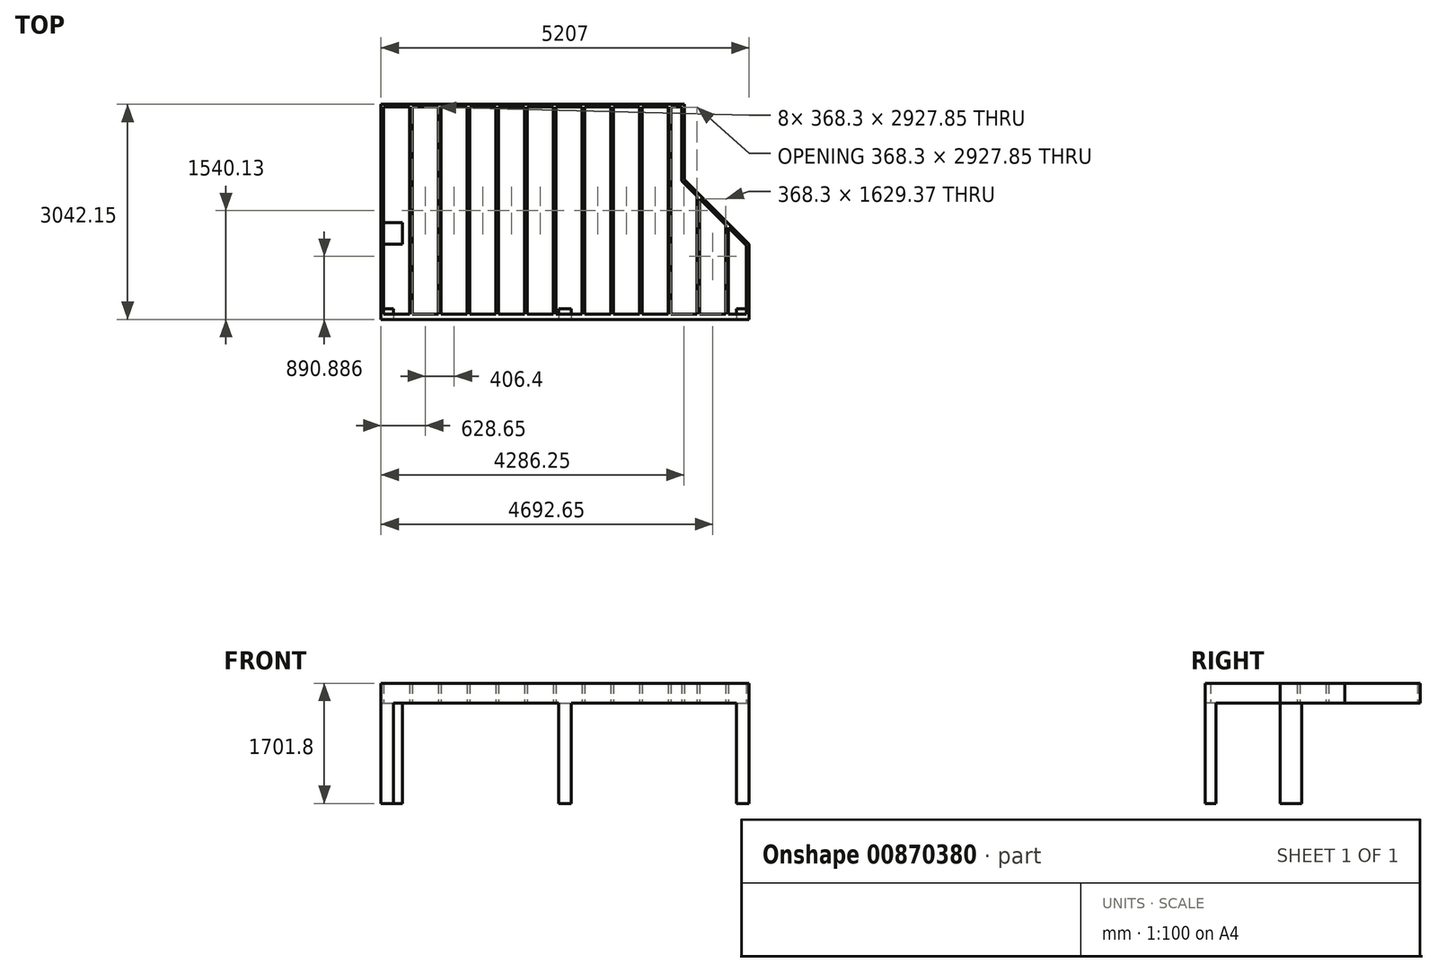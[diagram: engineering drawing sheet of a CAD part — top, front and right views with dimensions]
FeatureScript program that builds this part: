
annotation { "Feature Type Name" : "Feature", "Feature Type Description" : "" }
export const myFeature = defineFeature(function(context is Context, id is Id, definition is map)
    precondition{}
    {
        {
            var Q0;
            Q0=qCreatedBy(makeId("Top.planeOp"),FACE);
            var sketch = newSketch(context, id + "F0", { "sketchPlane" : qUnion([Q0])});
            skLineSegment(sketch, "E0.bottom", {"start": v(0, -1676.4) * mm, "end": v(304.8, -1676.4) * mm});
            skLineSegment(sketch, "E0.top", {"start": v(0, -1981.2) * mm, "end": v(304.8, -1981.2) * mm});
            skLineSegment(sketch, "E0.left", {"start": v(0, -1676.4) * mm, "end": v(0, -1981.2) * mm});
            skLineSegment(sketch, "E0.right", {"start": v(304.8, -1676.4) * mm, "end": v(304.8, -1981.2) * mm});
            skLineSegment(sketch, "E1.bottom", {"start": v(0, -2889.75) * mm, "end": v(177.8, -2889.75) * mm});
            skLineSegment(sketch, "E1.top", {"start": v(0, -3042.15) * mm, "end": v(177.8, -3042.15) * mm});
            skLineSegment(sketch, "E1.left", {"start": v(0, -2889.75) * mm, "end": v(0, -3042.15) * mm});
            skLineSegment(sketch, "E1.right", {"start": v(177.8, -2889.75) * mm, "end": v(177.8, -3042.15) * mm});
            skLineSegment(sketch, "E2.bottom", {"start": v(2514.6, -2889.75) * mm, "end": v(2692.4, -2889.75) * mm});
            skLineSegment(sketch, "E2.top", {"start": v(2514.6, -3042.15) * mm, "end": v(2692.4, -3042.15) * mm});
            skLineSegment(sketch, "E2.left", {"start": v(2514.6, -2889.75) * mm, "end": v(2514.6, -3042.15) * mm});
            skLineSegment(sketch, "E2.right", {"start": v(2692.4, -2889.75) * mm, "end": v(2692.4, -3042.15) * mm});
            skLineSegment(sketch, "E3.bottom", {"start": v(5029.2, -2889.75) * mm, "end": v(5207, -2889.75) * mm});
            skLineSegment(sketch, "E3.top", {"start": v(5029.2, -3042.15) * mm, "end": v(5207, -3042.15) * mm});
            skLineSegment(sketch, "E3.left", {"start": v(5029.2, -2889.75) * mm, "end": v(5029.2, -3042.15) * mm});
            skLineSegment(sketch, "E3.right", {"start": v(5207, -2889.75) * mm, "end": v(5207, -3042.15) * mm});
            skLineSegment(sketch, "E4", {"start": v(0, 0) * mm, "end": v(4292.6, 0) * mm, "construction": true});
            skLineSegment(sketch, "E5", {"start": v(4292.6, 0) * mm, "end": v(4292.6, -1066.8) * mm, "construction": true});
            skLineSegment(sketch, "E6", {"start": v(4292.6, -1066.8) * mm, "end": v(5226.55, -2000.75) * mm, "construction": true});
            skLineSegment(sketch, "E7", {"start": v(5226.55, -2000.75) * mm, "end": v(7106.15, -2000.75) * mm, "construction": true});
            skSolve(sketch);
        }
        {
            var Q0;
            Q0 = qSketchRegion(id + "F0", true);
            extrude(context, id + "F1", {"entities" : qUnion([Q0]), "depth" : 1422.4 * mm, "offsetDistance" : 25.4 * mm});
        }
        {
            var Q0;
            Q0=makeQuery(id+"F1.opExtrude","CAP_FACE",FACE,{"disambiguationData":[OSD([sQuery(id+"F0.wireOp",EDGE,"E0.bottom"),sQuery(id+"F0.wireOp",EDGE,"E0.top"),sQuery(id+"F0.wireOp",EDGE,"E0.left"),sQuery(id+"F0.wireOp",EDGE,"E0.right")])],"isStart":false});
            var sketch = newSketch(context, id + "F2", { "sketchPlane" : qUnion([Q0])});
            skLineSegment(sketch, "E8.0", {"start": v(0, 0) * mm, "end": v(4292.6, 0) * mm});
            skLineSegment(sketch, "E9.0", {"start": v(4292.6, 0) * mm, "end": v(4292.6, -1066.8) * mm});
            skLineSegment(sketch, "E9.1", {"start": v(4292.6, -1066.8) * mm, "end": v(5207, -1981.2) * mm});
            skLineSegment(sketch, "E10", {"start": v(0, 0) * mm, "end": v(0, -3042.15) * mm});
            skLineSegment(sketch, "E11", {"start": v(0, -3042.15) * mm, "end": v(5207, -3042.15) * mm});
            skLineSegment(sketch, "E12", {"start": v(5207, -3042.15) * mm, "end": v(5207, -1981.2) * mm});
            skPoint(sketch, "E13.orphan", {"position": v(5226.55, -2000.75) * mm});
            skLineSegment(sketch, "E14.0", {"start": v(4254.5, -38.1) * mm, "end": v(4254.5, -1082.58) * mm});
            skLineSegment(sketch, "E14.1", {"start": v(5168.9, -3004.05) * mm, "end": v(5168.9, -1996.98) * mm});
            skLineSegment(sketch, "E14.2", {"start": v(38.1, -3004.05) * mm, "end": v(5168.9, -3004.05) * mm});
            skLineSegment(sketch, "E14.3", {"start": v(4254.5, -1082.58) * mm, "end": v(5168.9, -1996.98) * mm});
            skLineSegment(sketch, "E14.4", {"start": v(38.1, -38.1) * mm, "end": v(38.1, -3004.05) * mm});
            skLineSegment(sketch, "E14.5", {"start": v(38.1, -38.1) * mm, "end": v(4254.5, -38.1) * mm});
            skSolve(sketch);
        }
        {
            var Q0;
            Q0 = qSketchRegion(id + "F2", true);
            extrude(context, id + "F3", {"entities" : qUnion([Q0]), "operationType" : NewBodyOperationType.ADD, "depth" : 279.4 * mm, "offsetDistance" : 25.4 * mm});
        }
        {
            var Q0;
            Q0=makeQuery(id+"F1.opExtrude","CAP_FACE",FACE,{"disambiguationData":[OSD([sQuery(id+"F0.wireOp",EDGE,"E1.bottom"),sQuery(id+"F0.wireOp",EDGE,"E1.top"),sQuery(id+"F0.wireOp",EDGE,"E1.left"),sQuery(id+"F0.wireOp",EDGE,"E1.right")])],"isStart":false});
            var sketch = newSketch(context, id + "F4", { "sketchPlane" : qUnion([Q0])});
            skPoint(sketch, "E15.oppositeSnap0", {"position": v(38.1, -2965.95) * mm});
            skLineSegment(sketch, "E15.bottom", {"start": v(38.1, -3004.05) * mm, "end": v(5168.9, -3004.05) * mm});
            skLineSegment(sketch, "E15.top", {"start": v(38.1, -2965.95) * mm, "end": v(5168.9, -2965.95) * mm});
            skLineSegment(sketch, "E15.left", {"start": v(38.1, -3004.05) * mm, "end": v(38.1, -2965.95) * mm});
            skLineSegment(sketch, "E15.right", {"start": v(5168.9, -3004.05) * mm, "end": v(5168.9, -2965.95) * mm});
            skSolve(sketch);
        }
        {
            var Q0;
            Q0 = qSketchRegion(id + "F4", true);
            var Q1;
            Q1=makeQuery(id+"F3.opExtrude","CAP_FACE",FACE,{"disambiguationData":[OSD([sQuery(id+"F2.wireOp",EDGE,"E8.0"),sQuery(id+"F2.wireOp",EDGE,"E9.0"),sQuery(id+"F2.wireOp",EDGE,"E9.1"),sQuery(id+"F2.wireOp",EDGE,"E10"),sQuery(id+"F2.wireOp",EDGE,"E11"),sQuery(id+"F2.wireOp",EDGE,"E12"),sQuery(id+"F2.wireOp",EDGE,"E14.0"),sQuery(id+"F2.wireOp",EDGE,"E14.1"),sQuery(id+"F2.wireOp",EDGE,"E14.2"),sQuery(id+"F2.wireOp",EDGE,"E14.3"),sQuery(id+"F2.wireOp",EDGE,"E14.4"),sQuery(id+"F2.wireOp",EDGE,"E14.5")])],"isStart":false});
            extrude(context, id + "F5", {"entities" : qUnion([Q0]), "operationType" : NewBodyOperationType.ADD, "endBound" : BoundingType.UP_TO_SURFACE, "depth" : 25.4 * mm, "endBoundEntityFace" : qUnion([Q1]), "offsetDistance" : 25.4 * mm});
        }
        {
            var Q0;
            Q0=makeQuery(id+"F1.opExtrude","CAP_FACE",FACE,{"disambiguationData":[OSD([sQuery(id+"F0.wireOp",EDGE,"E0.bottom"),sQuery(id+"F0.wireOp",EDGE,"E0.top"),sQuery(id+"F0.wireOp",EDGE,"E0.left"),sQuery(id+"F0.wireOp",EDGE,"E0.right")])],"isStart":false});
            var sketch = newSketch(context, id + "F6", { "sketchPlane" : qUnion([Q0])});
            skLineSegment(sketch, "E16.bottom", {"start": v(406.4, -38.1) * mm, "end": v(444.5, -38.1) * mm});
            skLineSegment(sketch, "E16.top", {"start": v(406.4, -2965.95) * mm, "end": v(444.5, -2965.95) * mm});
            skLineSegment(sketch, "E16.left", {"start": v(406.4, -38.1) * mm, "end": v(406.4, -2965.95) * mm});
            skLineSegment(sketch, "E16.right", {"start": v(444.5, -38.1) * mm, "end": v(444.5, -2965.95) * mm});
            skLineSegment(sketch, "E17.1.0.0", {"start": v(850.9, -38.1) * mm, "end": v(850.9, -2965.95) * mm});
            skLineSegment(sketch, "E17.1.0.1", {"start": v(812.8, -38.1) * mm, "end": v(812.8, -2965.95) * mm});
            skLineSegment(sketch, "E17.1.0.2", {"start": v(812.8, -38.1) * mm, "end": v(850.9, -38.1) * mm});
            skLineSegment(sketch, "E17.1.0.3", {"start": v(812.8, -2965.95) * mm, "end": v(850.9, -2965.95) * mm});
            skLineSegment(sketch, "E17.2.0.0", {"start": v(1257.3, -38.1) * mm, "end": v(1257.3, -2965.95) * mm});
            skLineSegment(sketch, "E17.2.0.1", {"start": v(1219.2, -38.1) * mm, "end": v(1219.2, -2965.95) * mm});
            skLineSegment(sketch, "E17.2.0.2", {"start": v(1219.2, -38.1) * mm, "end": v(1257.3, -38.1) * mm});
            skLineSegment(sketch, "E17.2.0.3", {"start": v(1219.2, -2965.95) * mm, "end": v(1257.3, -2965.95) * mm});
            skLineSegment(sketch, "E17.3.0.0", {"start": v(1663.7, -38.1) * mm, "end": v(1663.7, -2965.95) * mm});
            skLineSegment(sketch, "E17.3.0.1", {"start": v(1625.6, -38.1) * mm, "end": v(1625.6, -2965.95) * mm});
            skLineSegment(sketch, "E17.3.0.2", {"start": v(1625.6, -38.1) * mm, "end": v(1663.7, -38.1) * mm});
            skLineSegment(sketch, "E17.3.0.3", {"start": v(1625.6, -2965.95) * mm, "end": v(1663.7, -2965.95) * mm});
            skLineSegment(sketch, "E17.4.0.0", {"start": v(2070.1, -38.1) * mm, "end": v(2070.1, -2965.95) * mm});
            skLineSegment(sketch, "E17.4.0.1", {"start": v(2032, -38.1) * mm, "end": v(2032, -2965.95) * mm});
            skLineSegment(sketch, "E17.4.0.2", {"start": v(2032, -38.1) * mm, "end": v(2070.1, -38.1) * mm});
            skLineSegment(sketch, "E17.4.0.3", {"start": v(2032, -2965.95) * mm, "end": v(2070.1, -2965.95) * mm});
            skLineSegment(sketch, "E17.5.0.0", {"start": v(2476.5, -38.1) * mm, "end": v(2476.5, -2965.95) * mm});
            skLineSegment(sketch, "E17.5.0.1", {"start": v(2438.4, -38.1) * mm, "end": v(2438.4, -2965.95) * mm});
            skLineSegment(sketch, "E17.5.0.2", {"start": v(2438.4, -38.1) * mm, "end": v(2476.5, -38.1) * mm});
            skLineSegment(sketch, "E17.5.0.3", {"start": v(2438.4, -2965.95) * mm, "end": v(2476.5, -2965.95) * mm});
            skLineSegment(sketch, "E17.6.0.0", {"start": v(2882.9, -38.1) * mm, "end": v(2882.9, -2965.95) * mm});
            skLineSegment(sketch, "E17.6.0.1", {"start": v(2844.8, -38.1) * mm, "end": v(2844.8, -2965.95) * mm});
            skLineSegment(sketch, "E17.6.0.2", {"start": v(2844.8, -38.1) * mm, "end": v(2882.9, -38.1) * mm});
            skLineSegment(sketch, "E17.6.0.3", {"start": v(2844.8, -2965.95) * mm, "end": v(2882.9, -2965.95) * mm});
            skLineSegment(sketch, "E17.7.0.0", {"start": v(3289.3, -38.1) * mm, "end": v(3289.3, -2965.95) * mm});
            skLineSegment(sketch, "E17.7.0.1", {"start": v(3251.2, -38.1) * mm, "end": v(3251.2, -2965.95) * mm});
            skLineSegment(sketch, "E17.7.0.2", {"start": v(3251.2, -38.1) * mm, "end": v(3289.3, -38.1) * mm});
            skLineSegment(sketch, "E17.7.0.3", {"start": v(3251.2, -2965.95) * mm, "end": v(3289.3, -2965.95) * mm});
            skLineSegment(sketch, "E17.8.0.0", {"start": v(3695.7, -38.1) * mm, "end": v(3695.7, -2965.95) * mm});
            skLineSegment(sketch, "E17.8.0.1", {"start": v(3657.6, -38.1) * mm, "end": v(3657.6, -2965.95) * mm});
            skLineSegment(sketch, "E17.8.0.2", {"start": v(3657.6, -38.1) * mm, "end": v(3695.7, -38.1) * mm});
            skLineSegment(sketch, "E17.8.0.3", {"start": v(3657.6, -2965.95) * mm, "end": v(3695.7, -2965.95) * mm});
            skLineSegment(sketch, "E17.9.0.0", {"start": v(4102.1, -38.1) * mm, "end": v(4102.1, -2965.95) * mm});
            skLineSegment(sketch, "E17.9.0.1", {"start": v(4064, -38.1) * mm, "end": v(4064, -2965.95) * mm});
            skLineSegment(sketch, "E17.9.0.2", {"start": v(4064, -38.1) * mm, "end": v(4102.1, -38.1) * mm});
            skLineSegment(sketch, "E17.9.0.3", {"start": v(4064, -2965.95) * mm, "end": v(4102.1, -2965.95) * mm});
            skLineSegment(sketch, "E17.direction1", {"start": v(406.4, -2965.95) * mm, "end": v(812.8, -2965.95) * mm, "construction": true});
            skLineSegment(sketch, "E18.top", {"start": v(4470.4, -2965.95) * mm, "end": v(4508.5, -2965.95) * mm});
            skLineSegment(sketch, "E18.left", {"start": v(4470.4, -1298.48) * mm, "end": v(4470.4, -2965.95) * mm});
            skLineSegment(sketch, "E18.right", {"start": v(4508.5, -1336.58) * mm, "end": v(4508.5, -2965.95) * mm});
            skLineSegment(sketch, "E19.top", {"start": v(4876.8, -2965.95) * mm, "end": v(4914.9, -2965.95) * mm});
            skLineSegment(sketch, "E19.left", {"start": v(4876.8, -1704.88) * mm, "end": v(4876.8, -2965.95) * mm});
            skLineSegment(sketch, "E19.right", {"start": v(4914.9, -1742.98) * mm, "end": v(4914.9, -2965.95) * mm});
            skLineSegment(sketch, "E20", {"start": v(4470.4, -1298.48) * mm, "end": v(4508.5, -1336.58) * mm});
            skLineSegment(sketch, "E21.trimOffspring", {"start": v(4876.8, -1704.88) * mm, "end": v(4914.9, -1742.98) * mm});
            skSolve(sketch);
        }
        {
            var Q0;
            Q0 = qSketchRegion(id + "F6", true);
            var Q1;
            {var subQ0=sQuery(id+"F2.wireOp",EDGE,"E14.5");var subQ1=sQuery(id+"F2.wireOp",EDGE,"E14.4");var subQ2=sQuery(id+"F2.wireOp",EDGE,"E14.3");var subQ3=sQuery(id+"F2.wireOp",EDGE,"E14.2");var subQ4=sQuery(id+"F2.wireOp",EDGE,"E14.1");var subQ5=sQuery(id+"F2.wireOp",EDGE,"E14.0");var subQ6=sQuery(id+"F2.wireOp",EDGE,"E12");var subQ7=sQuery(id+"F2.wireOp",EDGE,"E11");var subQ8=sQuery(id+"F2.wireOp",EDGE,"E10");var subQ9=sQuery(id+"F2.wireOp",EDGE,"E9.1");var subQ10=sQuery(id+"F2.wireOp",EDGE,"E9.0");var subQ11=sQuery(id+"F2.wireOp",EDGE,"E8.0");Q1=makeQuery(id+"F5.boolean.opBoolean","MERGE",FACE,{"derivedFrom":[makeQuery(id+"F3.opExtrude","CAP_FACE",FACE,{"disambiguationData":[OSD([subQ11,subQ10,subQ9,subQ8,subQ7,subQ6,subQ5,subQ4,subQ3,subQ2,subQ1,subQ0])],"isStart":false}),makeQuery(id+"F5.opExtrude","CAP_FACE",FACE,{"disambiguationData":[OSD([subQ11,subQ10,subQ9,subQ8,subQ7,subQ6,subQ5,subQ4,subQ3,subQ2,subQ1,subQ0])],"isStart":false})]});}
            extrude(context, id + "F7", {"entities" : qUnion([Q0]), "operationType" : NewBodyOperationType.ADD, "endBound" : BoundingType.UP_TO_SURFACE, "depth" : 25.4 * mm, "endBoundEntityFace" : qUnion([Q1]), "offsetDistance" : 25.4 * mm});
        }
    });
